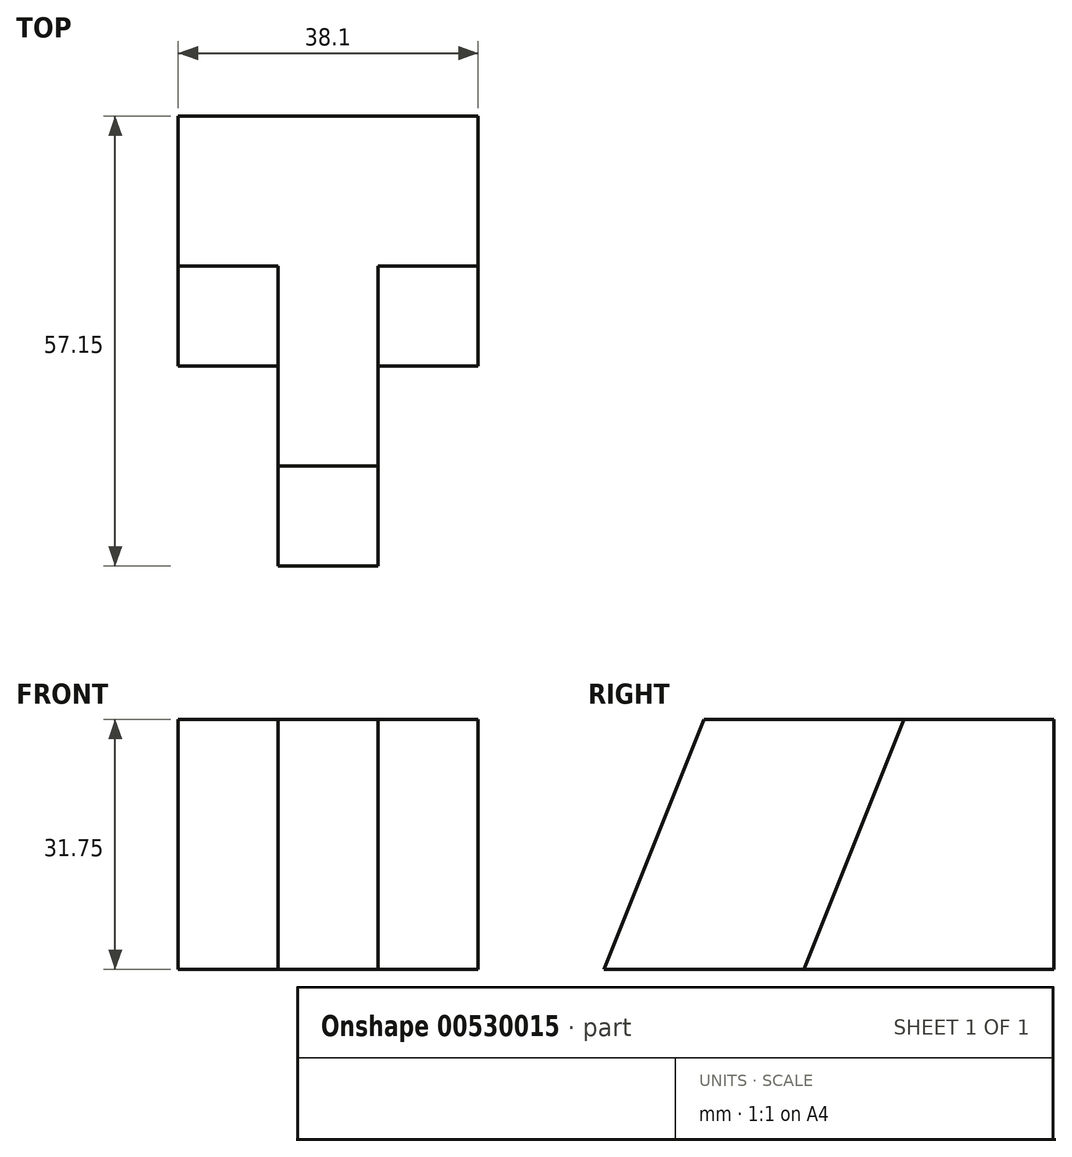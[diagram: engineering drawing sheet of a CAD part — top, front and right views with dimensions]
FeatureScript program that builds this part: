
annotation { "Feature Type Name" : "Feature", "Feature Type Description" : "" }
export const myFeature = defineFeature(function(context is Context, id is Id, definition is map)
    precondition{}
    {
        {
            var Q0;
            Q0=qCreatedBy(makeId("Top.planeOp"),FACE);
            var sketch = newSketch(context, id + "F0", { "sketchPlane" : qUnion([Q0])});
            skLineSegment(sketch, "E0", {"start": v(-61.43, 69.44) * mm, "end": v(-23.33, 69.44) * mm});
            skLineSegment(sketch, "E1", {"start": v(-61.43, 69.44) * mm, "end": v(-61.43, 37.69) * mm});
            skLineSegment(sketch, "E2", {"start": v(-23.33, 69.44) * mm, "end": v(-23.33, 37.69) * mm});
            skLineSegment(sketch, "E3", {"start": v(-61.43, 37.69) * mm, "end": v(-48.73, 37.69) * mm});
            skLineSegment(sketch, "E4", {"start": v(-48.73, 37.69) * mm, "end": v(-48.73, 12.29) * mm});
            skLineSegment(sketch, "E5", {"start": v(-48.73, 12.29) * mm, "end": v(-36.03, 12.29) * mm});
            skLineSegment(sketch, "E6", {"start": v(-36.03, 12.29) * mm, "end": v(-36.03, 37.69) * mm});
            skLineSegment(sketch, "E7", {"start": v(-36.03, 37.69) * mm, "end": v(-23.33, 37.69) * mm});
            skSolve(sketch);
        }
        {
            var Q0;
            Q0=makeQuery(id+"F0.imprint","IMPRINT",FACE,{"disambiguationData":[TD([[makeQuery(id+"F0.imprint","IMPRINT",EDGE,{"derivedFrom":sQuery(id+"F0.wireOp",EDGE,"E0")}),-1.0]])]});
            extrude(context, id + "F1", {"entities" : qUnion([Q0]), "depth" : 31.75 * mm, "offsetDistance" : 25.4 * mm});
        }
        {
            var Q0;
            Q0=makeQuery(id+"F1.opExtrude","SWEPT_FACE",FACE,{"disambiguationData":[OSD([sQuery(id+"F0.wireOp",EDGE,"E2")])]});
            var sketch = newSketch(context, id + "F2", { "sketchPlane" : qUnion([Q0])});
            skLineSegment(sketch, "E8", {"start": v(37.69, 0) * mm, "end": v(50.39, 31.75) * mm});
            skLineSegment(sketch, "E9", {"start": v(37.69, 31.75) * mm, "end": v(50.39, 31.75) * mm});
            skLineSegment(sketch, "E10", {"start": v(37.69, 31.75) * mm, "end": v(37.69, 0) * mm});
            skSolve(sketch);
        }
        {
            var Q0;
            Q0=makeQuery(id+"F2.imprint","IMPRINT",FACE,{"disambiguationData":[TD([[makeQuery(id+"F2.imprint","IMPRINT",EDGE,{"derivedFrom":sQuery(id+"F2.wireOp",EDGE,"E8")}),1.0]])]});
            extrude(context, id + "F3", {"entities" : qUnion([Q0]), "operationType" : NewBodyOperationType.REMOVE, "oppositeDirection" : true, "depth" : 12.7 * mm, "offsetDistance" : 25.4 * mm});
        }
        {
            var Q0;
            Q0=makeQuery(id+"F1.opExtrude","SWEPT_FACE",FACE,{"disambiguationData":[OSD([sQuery(id+"F0.wireOp",EDGE,"E1")])]});
            var sketch = newSketch(context, id + "F4", { "sketchPlane" : qUnion([Q0])});
            skLineSegment(sketch, "E11", {"start": v(-37.69, 0) * mm, "end": v(-50.39, 31.75) * mm});
            skLineSegment(sketch, "E12", {"start": v(-50.39, 31.75) * mm, "end": v(-37.69, 31.75) * mm});
            skLineSegment(sketch, "E13", {"start": v(-37.69, 31.75) * mm, "end": v(-37.69, 0) * mm});
            skSolve(sketch);
        }
        {
            var Q0;
            Q0=makeQuery(id+"F4.imprint","IMPRINT",FACE,{"disambiguationData":[TD([[makeQuery(id+"F4.imprint","IMPRINT",EDGE,{"derivedFrom":sQuery(id+"F4.wireOp",EDGE,"E11")}),-1.0]])]});
            extrude(context, id + "F5", {"entities" : qUnion([Q0]), "operationType" : NewBodyOperationType.REMOVE, "oppositeDirection" : true, "depth" : 12.7 * mm, "offsetDistance" : 25.4 * mm});
        }
        {
            var Q0;
            Q0=makeQuery(id+"F3.boolean.opBoolean","MERGE",FACE,{"derivedFrom":[makeQuery(id+"F1.opExtrude","SWEPT_FACE",FACE,{"disambiguationData":[OSD([sQuery(id+"F0.wireOp",EDGE,"E6")])]}),makeQuery(id+"F3.opExtrude","CAP_FACE",FACE,{"disambiguationData":[OSD([sQuery(id+"F2.wireOp",EDGE,"E8"),sQuery(id+"F2.wireOp",EDGE,"E9"),sQuery(id+"F2.wireOp",EDGE,"E10")])],"isStart":false})]});
            var sketch = newSketch(context, id + "F6", { "sketchPlane" : qUnion([Q0])});
            skLineSegment(sketch, "E14", {"start": v(12.29, 0) * mm, "end": v(24.99, 31.75) * mm});
            skLineSegment(sketch, "E15", {"start": v(12.29, 31.75) * mm, "end": v(24.99, 31.75) * mm});
            skLineSegment(sketch, "E16", {"start": v(12.29, 31.75) * mm, "end": v(12.29, 0) * mm});
            skSolve(sketch);
        }
        {
            var Q0;
            Q0=makeQuery(id+"F6.imprint","IMPRINT",FACE,{"disambiguationData":[TD([[makeQuery(id+"F6.imprint","IMPRINT",EDGE,{"derivedFrom":sQuery(id+"F6.wireOp",EDGE,"E14")}),1.0]])]});
            extrude(context, id + "F7", {"entities" : qUnion([Q0]), "operationType" : NewBodyOperationType.REMOVE, "oppositeDirection" : true, "depth" : 12.7 * mm, "offsetDistance" : 25.4 * mm});
        }
    });
